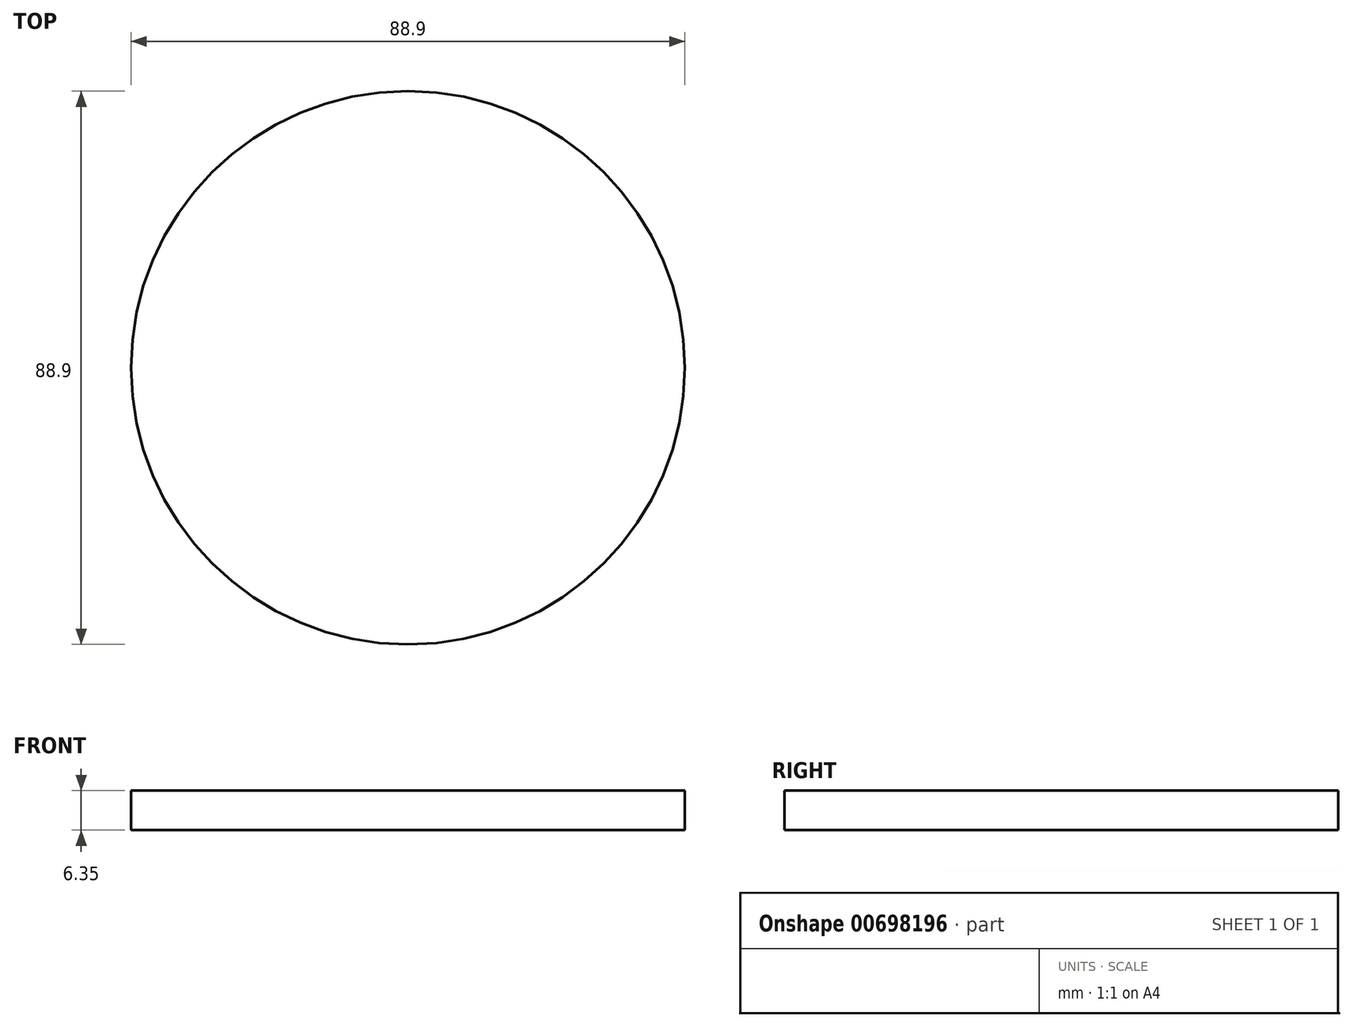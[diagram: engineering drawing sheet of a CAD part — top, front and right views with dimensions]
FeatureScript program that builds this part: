
annotation { "Feature Type Name" : "Feature", "Feature Type Description" : "" }
export const myFeature = defineFeature(function(context is Context, id is Id, definition is map)
    precondition{}
    {
        {
            var Q0;
            Q0=qCreatedBy(makeId("Top.planeOp"),FACE);
            var sketch = newSketch(context, id + "F0", { "sketchPlane" : qUnion([Q0])});
            skCircle(sketch, "E0", {"center": v(0, 0) * mm, "radius": 44.45 * mm});
            skSolve(sketch);
        }
        {
            var Q0;
            Q0=makeQuery(id+"F0.imprint","IMPRINT",FACE,{"disambiguationData":[TD([[makeQuery(id+"F0.imprint","IMPRINT",EDGE,{"derivedFrom":sQuery(id+"F0.wireOp",EDGE,"E0")}),1.0]])]});
            extrude(context, id + "F1", {"entities" : qUnion([Q0]), "depth" : 6.35 * mm, "offsetDistance" : 25.4 * mm});
        }
    });
